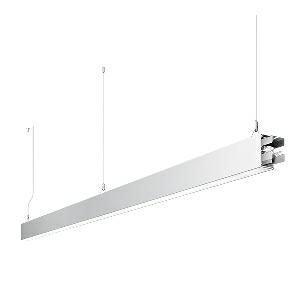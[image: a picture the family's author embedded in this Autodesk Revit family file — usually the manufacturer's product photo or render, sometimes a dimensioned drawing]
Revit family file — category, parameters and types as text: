
# Revit family: idoo_line_-_ilp_6000_830_d_sta_00805743_ab75
name_source: partatom
category: Lighting Fixtures
units: mm (PartAtom-declared; Revit-internal decimal feet)

## family parameters
Cut with Voids When Loaded = No
Host = Face
Light Source = No
Part Type = Normal
Room Calculation Point = No
Round Connector Dimension = Use Diameter
Shared = No

## types (1)
- IDOO.line - ILP 6000/830/D STA (1 x LED, 6000 lm, 3000K)
    Apparent Load = 46 VA
    Approval mark = CE
    CIE Flux Codes = 66 91 98 40 100
    Color Rendering = 80-89
    Color Temperature = 3000K
    Control Gear = Electronic ballast
    Default Elevation = 1800 mm
    Description = ILP 6000/830/D|Suspended luminaire|light source: LED|connected load: 220-240 V, 50/60 Hz|Power consumption: approx. 46 W|standby: approx. 0,15|luminous flux: 6000 lm|luminous efficacy: 130 lm/W|light distribution: Direct/indirect|direct ratio: approx. 40 %|colour temperature: Warm white, ca. 3000 K|color rendering index (CRI): >= 80|chromaticity tolerance:  3 SDCM|System of protection: IP 40|technology: Continuously dimmable|luminaire body|material: Sectional aluminium|colour: White|lamp cover: Acrylic (PMMA), Clear|mains lead: 2.00 m With free stranded wires|Fastening: Steel cable 0.3 - 0.7 m|glare control: Prism aperture|luminance(L65): <= 2700 cd/m|unified glare rating(4H 8H): <=  16|special features: DALI Load 1x, TouchDIM - dimming via standard switch, Through-wired, up to 18 m on one mains connection, Flicker-free, Suitable as emergency lighting, Start luminaire with mains connection, Mechanical and electrical connection of the individual modules without tools|
    Frequency = 50 Hz
    Height = 110 mm
    Lamp = 1 x LED
    Lamp Light Flux = 6000 lm
    Lamp count = 1
    Length = 2250 mm
    Luminous efficacy = 130 lm/W
    Manufacturer = Waldmann
    ModVariant = No
    Model = 00805743
    Mounting Place = Ceiling
    Mounting Type = Pendant
    Number of Poles = 1
    OnlyDefault = Yes
    Power Factor = 1
    Product Name = IDOO.line - ILP 6000/830/D STA
    Product group = Suspended luminaire
    ProductGroupID = 9
    Protection Class = Protection class I
    Protection Degree = IP 40
    RLX_Detail_Level = 1
    RLX_Emergency_Light_Flux = 0 lm
    RLX_Emergency_Type = 0
    RLX_Emergency_Type_DB = No
    RlxData = <blob elided: 22909 chars, md5=98b6220c>
    Socket = socket
    Standby Power = 0 W
    System Light Flux = 6000 lm
    System Power = 46 W
    Type Comments = Product without accessories
    Type Image = 113313000-00692603.jpg
    URL = http://relux.com
    VarID = ---
    Voltage = 230 V
    Voltage Range = 220-240 V
    Weight = 0.00 kg
    Width = 60 mm  [stored 0.19685 ft]

note: [stored X ft] marks values corroborated as IEEE doubles in the binary element streams (Revit-internal decimal feet)

## geometry (parser evidence)
native form markers: Blend x4, Sweep x12
no freeform markers — native parametric forms only
